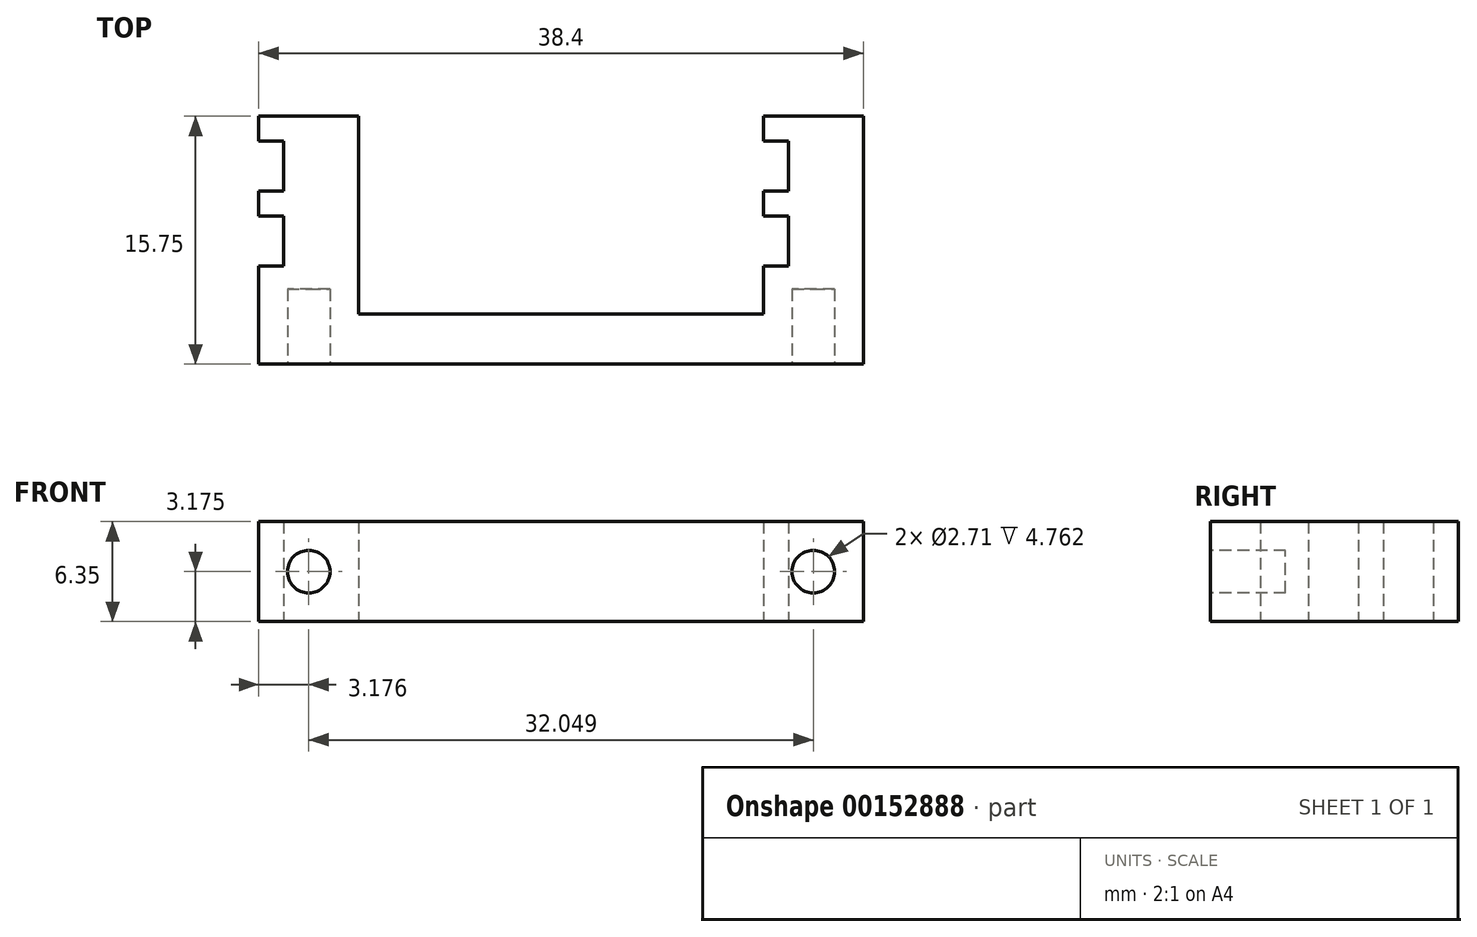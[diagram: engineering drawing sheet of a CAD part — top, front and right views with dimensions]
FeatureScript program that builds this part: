
annotation { "Feature Type Name" : "Feature", "Feature Type Description" : "" }
export const myFeature = defineFeature(function(context is Context, id is Id, definition is map)
    precondition{}
    {
        {
            var Q0;
            Q0=qCreatedBy(makeId("Top.planeOp"),FACE);
            var sketch = newSketch(context, id + "F0", { "sketchPlane" : qUnion([Q0])});
            skLineSegment(sketch, "E0.bottom", {"start": v(0, 0) * mm, "end": v(1.59, 0) * mm});
            skLineSegment(sketch, "E0.top", {"start": v(0, -3.18) * mm, "end": v(1.59, -3.18) * mm});
            skLineSegment(sketch, "E0.left", {"start": v(0, 0) * mm, "end": v(0, -3.18) * mm, "construction": true});
            skLineSegment(sketch, "E0.right", {"start": v(1.59, 0) * mm, "end": v(1.59, -3.18) * mm});
            skLineSegment(sketch, "E1", {"start": v(0, -3.18) * mm, "end": v(0, -4.76) * mm});
            skLineSegment(sketch, "E2.top", {"start": v(0, 1.59) * mm, "end": v(6.35, 1.59) * mm});
            skLineSegment(sketch, "E2.left", {"start": v(0, 0) * mm, "end": v(0, 1.59) * mm});
            skLineSegment(sketch, "E2.right", {"start": v(6.35, -14.16) * mm, "end": v(6.35, 1.59) * mm});
            skLineSegment(sketch, "E3.bottom", {"start": v(0, -4.76) * mm, "end": v(1.59, -4.76) * mm});
            skLineSegment(sketch, "E3.top", {"start": v(0, -7.94) * mm, "end": v(1.59, -7.94) * mm});
            skLineSegment(sketch, "E3.left", {"start": v(0, -4.76) * mm, "end": v(0, -7.94) * mm, "construction": true});
            skLineSegment(sketch, "E3.right", {"start": v(1.59, -4.76) * mm, "end": v(1.59, -7.94) * mm});
            skLineSegment(sketch, "E4", {"start": v(0, -7.94) * mm, "end": v(0, -10.99) * mm});
            skLineSegment(sketch, "E5", {"start": v(0, -10.99) * mm, "end": v(-25.7, -10.99) * mm});
            skLineSegment(sketch, "E6.bottom", {"start": v(-30.46, -7.94) * mm, "end": v(-32.05, -7.94) * mm});
            skLineSegment(sketch, "E6.top", {"start": v(-30.46, -4.76) * mm, "end": v(-32.05, -4.76) * mm});
            skLineSegment(sketch, "E6.left", {"start": v(-32.05, -7.94) * mm, "end": v(-32.05, -4.76) * mm, "construction": true});
            skLineSegment(sketch, "E6.right", {"start": v(-30.46, -7.94) * mm, "end": v(-30.46, -4.76) * mm});
            skLineSegment(sketch, "E7", {"start": v(-32.05, -4.76) * mm, "end": v(-32.05, -3.18) * mm});
            skLineSegment(sketch, "E8.bottom", {"start": v(-30.46, -3.18) * mm, "end": v(-32.05, -3.18) * mm});
            skLineSegment(sketch, "E8.top", {"start": v(-30.46, 0) * mm, "end": v(-32.05, 0) * mm});
            skLineSegment(sketch, "E8.left", {"start": v(-32.05, -3.18) * mm, "end": v(-32.05, 0) * mm, "construction": true});
            skLineSegment(sketch, "E8.right", {"start": v(-30.46, -3.18) * mm, "end": v(-30.46, 0) * mm});
            skLineSegment(sketch, "E9", {"start": v(-32.05, 0) * mm, "end": v(-32.05, 1.59) * mm});
            skLineSegment(sketch, "E10", {"start": v(-25.7, 1.59) * mm, "end": v(-32.05, 1.59) * mm});
            skLineSegment(sketch, "E11", {"start": v(-25.7, 1.59) * mm, "end": v(-25.7, -10.99) * mm});
            skLineSegment(sketch, "E12", {"start": v(-32.05, -7.94) * mm, "end": v(-32.05, -14.16) * mm});
            skLineSegment(sketch, "E13", {"start": v(-32.05, -14.16) * mm, "end": v(6.35, -14.16) * mm});
            skLineSegment(sketch, "E14", {"start": v(-12.85, -10.99) * mm, "end": v(-12.85, -14.16) * mm, "construction": true});
            skSolve(sketch);
        }
        {
            var Q0;
            Q0 = qSketchRegion(id + "F0", true);
            extrude(context, id + "F1", {"entities" : qUnion([Q0]), "depth" : 6.35 * mm});
        }
        {
            var Q0;
            Q0=makeQuery(id+"F1.opExtrude","SWEPT_FACE",FACE,{"disambiguationData":[OSD([sQuery(id+"F0.wireOp",EDGE,"E13")])]});
            var sketch = newSketch(context, id + "F2", { "sketchPlane" : qUnion([Q0])});
            skLineSegment(sketch, "E15.bottom", {"start": v(-32.05, 3.18) * mm, "end": v(-28.87, 3.18) * mm, "construction": true});
            skLineSegment(sketch, "E15.top", {"start": v(-32.05, 0) * mm, "end": v(-28.87, 0) * mm, "construction": true});
            skLineSegment(sketch, "E15.left", {"start": v(-32.05, 3.18) * mm, "end": v(-32.05, 0) * mm, "construction": true});
            skLineSegment(sketch, "E15.right", {"start": v(-28.87, 3.18) * mm, "end": v(-28.87, 0) * mm, "construction": true});
            skLineSegment(sketch, "E16.bottom", {"start": v(6.35, 3.18) * mm, "end": v(3.18, 3.18) * mm, "construction": true});
            skLineSegment(sketch, "E16.top", {"start": v(6.35, 0) * mm, "end": v(3.18, 0) * mm, "construction": true});
            skLineSegment(sketch, "E16.left", {"start": v(6.35, 3.18) * mm, "end": v(6.35, 0) * mm, "construction": true});
            skLineSegment(sketch, "E16.right", {"start": v(3.18, 3.18) * mm, "end": v(3.18, 0) * mm, "construction": true});
            skCircle(sketch, "E17", {"center": v(-28.87, 3.18) * mm, "radius": 1.35 * mm});
            skCircle(sketch, "E18", {"center": v(3.18, 3.18) * mm, "radius": 1.35 * mm});
            skSolve(sketch);
        }
        {
            var Q0;
            Q0 = qSketchRegion(id + "F2", true);
            extrude(context, id + "F3", {"entities" : qUnion([Q0]), "operationType" : NewBodyOperationType.REMOVE, "oppositeDirection" : true, "depth" : 4.76 * mm});
        }
    });
